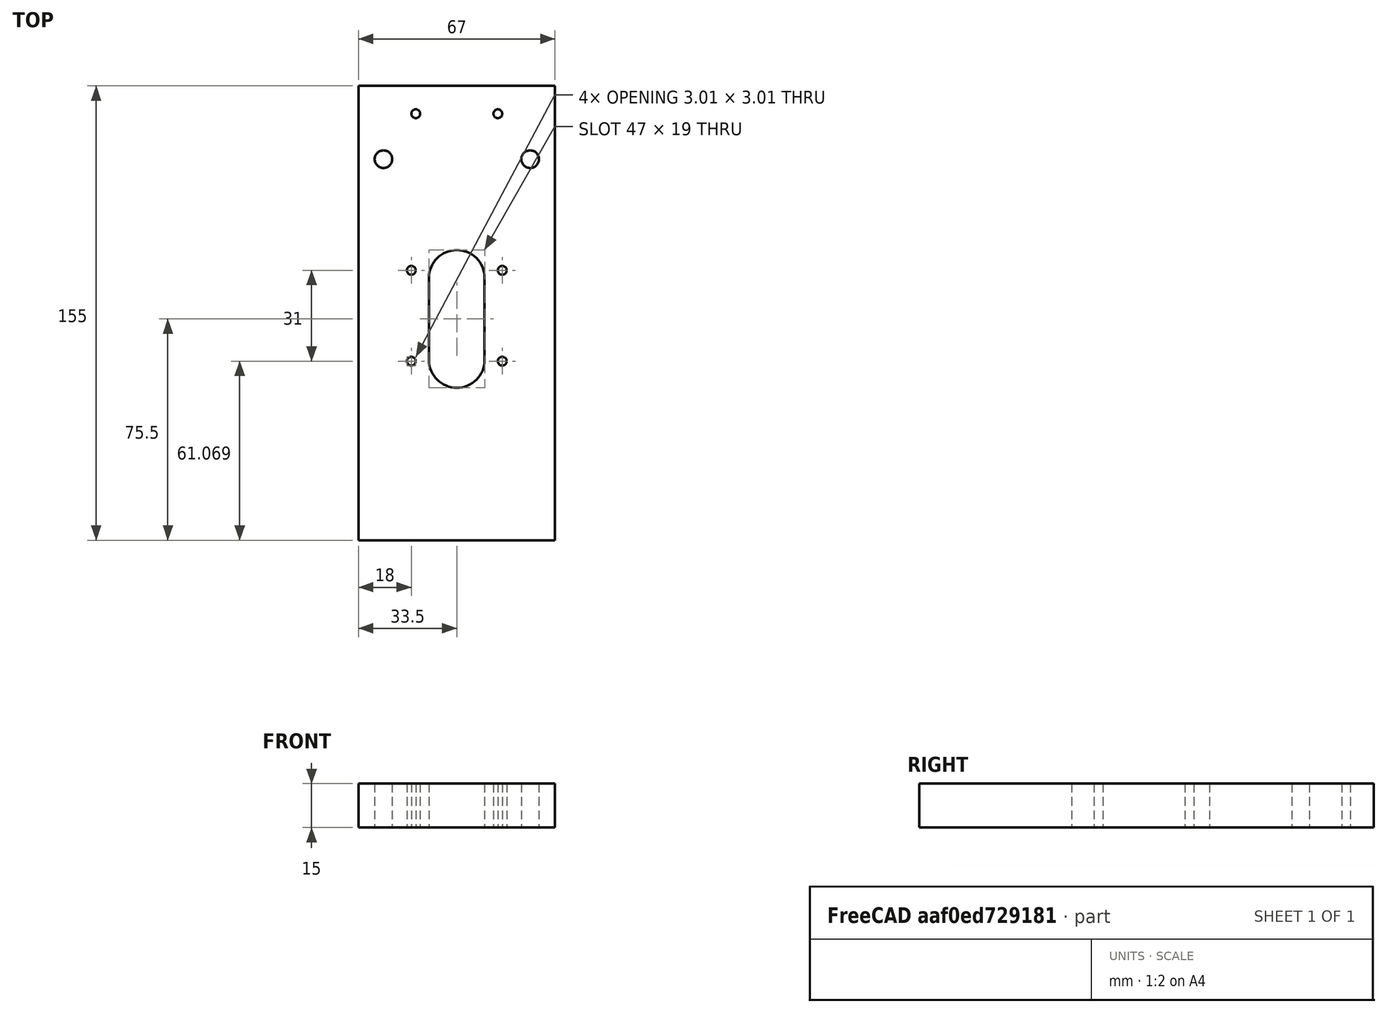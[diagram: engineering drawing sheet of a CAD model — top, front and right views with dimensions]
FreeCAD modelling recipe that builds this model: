
FCSTD DOCUMENT  (FreeCAD 0.19R)
Label: planche_support_moteur_x
License: All rights reserved
LicenseURL: http://en.wikipedia.org/wiki/All_rights_reserved
objects: Part::Feature×1, PartDesign::ShapeBinder×1, Sketcher::SketchObject×1, PartDesign::Body×1
note: 4 computed .brp shape members not serialized (recipe doc carries the construction recipe); baked Part::Feature solids carry a one-line shape summary decoded from their .brp

FEATURE [Part::Feature] Part__Feature  label="planche support moteur x"
  shape: bbox 67 x 155 x 15 mm, 26 faces (baked)
FEATURE [PartDesign::ShapeBinder] CopyPart__Feature
  TraceSupport = false
FEATURE [Sketcher::SketchObject] Sketch
  FullyConstrained = false
  MapMode = 5
  Placement = pos=(0,0,0) rot=(1,0,0;3.14159rad)
  Support = -> [CopyPart__Feature]
  sketch-geometry (4):
    g0: LineSegment StartX=-21.0326 StartY=85.9093 StartZ=0 EndX=21.2472 EndY=85.9093 EndZ=0
    g1: LineSegment StartX=21.2472 StartY=85.9093 StartZ=0 EndX=21.2472 EndY=24.9287 EndZ=0
    g2: LineSegment StartX=21.2472 StartY=24.9287 StartZ=0 EndX=-21.0326 EndY=24.9287 EndZ=0
    g3: LineSegment StartX=-21.0326 StartY=24.9287 StartZ=0 EndX=-21.0326 EndY=85.9093 EndZ=0
  constraints (8):
    c: Coincident(g0,g1)
    c: Coincident(g1,g2)
    c: Coincident(g2,g3)
    c: Coincident(g3,g0)
    c: Horizontal(g0)
    c: Horizontal(g2)
    c: Vertical(g1)
    c: Vertical(g3)
FEATURE [PartDesign::Body] Body
  Group = -> [CopyPart__Feature,Sketch]
  Origin = -> Origin
